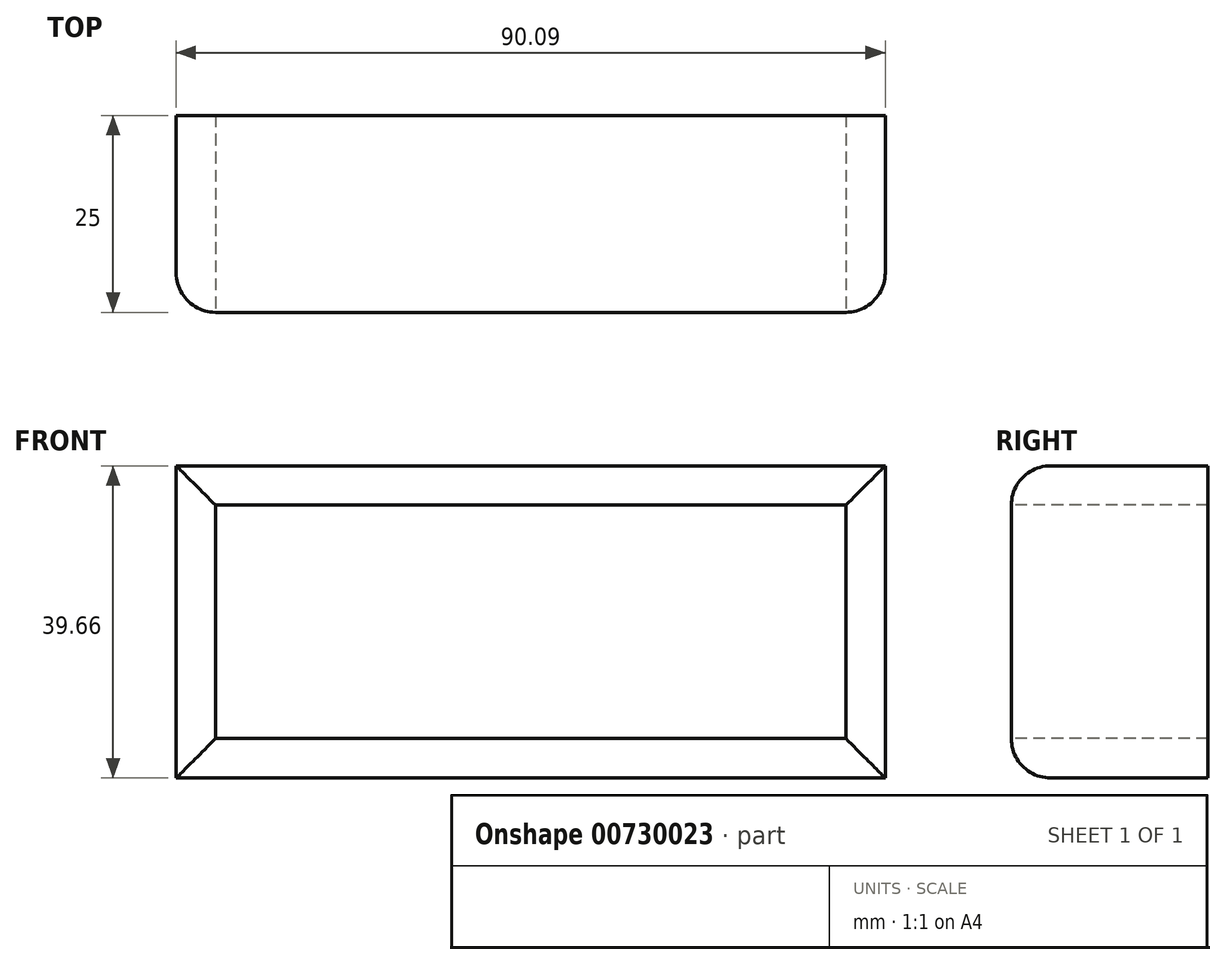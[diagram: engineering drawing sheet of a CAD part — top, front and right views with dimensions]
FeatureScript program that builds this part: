
annotation { "Feature Type Name" : "Feature", "Feature Type Description" : "" }
export const myFeature = defineFeature(function(context is Context, id is Id, definition is map)
    precondition{}
    {
        {
            var Q0;
            Q0=qCreatedBy(makeId("Front.planeOp"),FACE);
            var sketch = newSketch(context, id + "F0", { "sketchPlane" : qUnion([Q0])});
            skLineSegment(sketch, "E0.bottom", {"start": v(50, 25) * mm, "end": v(-50, 25) * mm});
            skLineSegment(sketch, "E0.top", {"start": v(50, -25) * mm, "end": v(-50, -25) * mm});
            skLineSegment(sketch, "E0.left", {"start": v(50, 25) * mm, "end": v(50, -25) * mm});
            skLineSegment(sketch, "E0.right", {"start": v(-50, 25) * mm, "end": v(-50, -25) * mm});
            skPoint(sketch, "E0.middle", {"position": v(0, 0) * mm});
            skSolve(sketch);
        }
        {
            var Q0;
            Q0=makeQuery(id+"F0.imprint","IMPRINT",FACE,{"disambiguationData":[TD([[makeQuery(id+"F0.imprint","IMPRINT",EDGE,{"derivedFrom":sQuery(id+"F0.wireOp",EDGE,"E0.bottom")}),1.0]])]});
            var sketch = newSketch(context, id + "F1", { "sketchPlane" : qUnion([Q0])});
            skSolve(sketch);
        }
        {
            var Q0;
            Q0 = qSketchRegion(id + "F1", true);
            var Q1;
            Q1=makeQuery(id+"F1.imprint","IMPRINT",FACE,{"disambiguationData":[TD([[makeQuery(id+"F1.imprint","IMPRINT",EDGE,{"derivedFrom":makeQuery(id+"F0.imprint","IMPRINT",EDGE,{"derivedFrom":sQuery(id+"F0.wireOp",EDGE,"E0.bottom")})}),1.0]])]});
            extrude(context, id + "F2", {"entities" : qUnion([Q0, Q1]), "depth" : 40 * mm, "offsetDistance" : 25 * mm});
        }
        {
            var Q0;
            Q0=makeQuery(id+"F2.opExtrude","CAP_FACE",FACE,{"disambiguationData":[OSD([sQuery(id+"F0.wireOp",EDGE,"E0.bottom"),sQuery(id+"F0.wireOp",EDGE,"E0.top"),sQuery(id+"F0.wireOp",EDGE,"E0.left"),sQuery(id+"F0.wireOp",EDGE,"E0.right")])],"isStart":false});
            var sketch = newSketch(context, id + "F3", { "sketchPlane" : qUnion([Q0])});
            skSolve(sketch);
        }
        {
            var Q0;
            Q0=makeQuery(id+"F3.imprint","IMPRINT",FACE,{"disambiguationData":[TD([[makeQuery(id+"F3.imprint","IMPRINT",EDGE,{"derivedFrom":makeQuery(id+"F2.opExtrude","CAP_EDGE",EDGE,{"disambiguationData":[OSD([sQuery(id+"F0.wireOp",EDGE,"E0.bottom")])],"isStart":false})}),1.0]])]});
            var sketch = newSketch(context, id + "F4", { "sketchPlane" : qUnion([Q0])});
            skLineSegment(sketch, "E1.bottom", {"start": v(45, 20) * mm, "end": v(-45, 20) * mm});
            skLineSegment(sketch, "E1.top", {"start": v(45, -20) * mm, "end": v(-45, -20) * mm});
            skLineSegment(sketch, "E1.left", {"start": v(45, 20) * mm, "end": v(45, -20) * mm});
            skLineSegment(sketch, "E1.right", {"start": v(-45, 20) * mm, "end": v(-45, -20) * mm});
            skPoint(sketch, "E1.middle", {"position": v(0, 0) * mm});
            skSolve(sketch);
        }
        {
            var Q0;
            Q0=makeQuery(id+"F4.imprint","IMPRINT",FACE,{"disambiguationData":[TD([[makeQuery(id+"F4.imprint","IMPRINT",EDGE,{"derivedFrom":sQuery(id+"F4.wireOp",EDGE,"E1.bottom")}),1.0]])]});
            extrude(context, id + "F5", {"entities" : qUnion([Q0]), "operationType" : NewBodyOperationType.REMOVE, "oppositeDirection" : true, "depth" : 36 * mm, "offsetDistance" : 25 * mm});
        }
        {
            var Q0;
            Q0=makeQuery(id+"F2.opExtrude","CAP_EDGE",EDGE,{"disambiguationData":[OSD([sQuery(id+"F0.wireOp",EDGE,"E0.right")])],"isStart":false});
            var Q1;
            Q1=makeQuery(id+"F2.opExtrude","CAP_EDGE",EDGE,{"disambiguationData":[OSD([sQuery(id+"F0.wireOp",EDGE,"E0.bottom")])],"isStart":false});
            var Q2;
            Q2=makeQuery(id+"F2.opExtrude","CAP_EDGE",EDGE,{"disambiguationData":[OSD([sQuery(id+"F0.wireOp",EDGE,"E0.left")])],"isStart":false});
            var Q3;
            Q3=makeQuery(id+"F2.opExtrude","CAP_EDGE",EDGE,{"disambiguationData":[OSD([sQuery(id+"F0.wireOp",EDGE,"E0.top")])],"isStart":false});
            fillet(context, id + "F6", {"entities" : qUnion([Q0, Q1, Q2, Q3]), "radius" : 5 * mm, "tangentPropagation" : true, "allowEdgeOverflow" : false});
        }
        {
            var Q0;
            Q0=makeQuery(id+"F3.imprint","IMPRINT",FACE,{"disambiguationData":[TD([[makeQuery(id+"F3.imprint","IMPRINT",EDGE,{"derivedFrom":makeQuery(id+"F2.opExtrude","CAP_EDGE",EDGE,{"disambiguationData":[OSD([sQuery(id+"F0.wireOp",EDGE,"E0.bottom")])],"isStart":false})}),1.0]])]});
            var sketch = newSketch(context, id + "F7", { "sketchPlane" : qUnion([Q0])});
            skSolve(sketch);
        }
        {
            var Q0;
            Q0=makeQuery(id+"F2.opExtrude","SWEPT_FACE",FACE,{"disambiguationData":[OSD([sQuery(id+"F0.wireOp",EDGE,"E0.top")])]});
            var sketch = newSketch(context, id + "F8", { "sketchPlane" : qUnion([Q0])});
            skText(sketch, "E2", { "text": "Jonas", "fontName": "OpenSans-Regular.ttf"});
            const initialGuessF8  = {"E2": [-0.0245, 0.01127, 1, 0, 0.01358]};
            skSetInitialGuess(sketch, initialGuessF8);
            skSolve(sketch);
        }
        {
            var Q0;
            Q0 = qSketchRegion(id + "F8", true);
            extrude(context, id + "F9", {"entities" : qUnion([Q0]), "operationType" : NewBodyOperationType.REMOVE, "oppositeDirection" : true, "depth" : 5.7 * mm, "offsetDistance" : 25 * mm});
        }
        {
            var Q0;
            Q0=makeQuery(id+"F7.imprint","IMPRINT",FACE,{"disambiguationData":[TD([[makeQuery(id+"F7.imprint","IMPRINT",EDGE,{"derivedFrom":makeQuery(id+"F3.imprint","IMPRINT",EDGE,{"derivedFrom":makeQuery(id+"F2.opExtrude","CAP_EDGE",EDGE,{"disambiguationData":[OSD([sQuery(id+"F0.wireOp",EDGE,"E0.bottom")])],"isStart":false})})}),1.0]])]});
            var sketch = newSketch(context, id + "F10", { "sketchPlane" : qUnion([Q0])});
            skLineSegment(sketch, "E3.bottom", {"start": v(-45.47, 19.97) * mm, "end": v(44.62, 19.97) * mm});
            skLineSegment(sketch, "E3.top", {"start": v(-45.47, -19.69) * mm, "end": v(44.62, -19.69) * mm});
            skLineSegment(sketch, "E3.left", {"start": v(-45.47, 19.97) * mm, "end": v(-45.47, -19.69) * mm});
            skLineSegment(sketch, "E3.right", {"start": v(44.62, 19.97) * mm, "end": v(44.62, -19.69) * mm});
            skSolve(sketch);
        }
        {
            var Q0;
            Q0 = qSketchRegion(id + "F10", true);
            extrude(context, id + "F11", {"entities" : qUnion([Q0]), "depth" : 25 * mm, "offsetDistance" : 25 * mm});
        }
        {
            var Q0;
            Q0=makeQuery(id+"F11.opExtrude","CAP_EDGE",EDGE,{"disambiguationData":[OSD([sQuery(id+"F10.wireOp",EDGE,"E3.top")])],"isStart":false});
            var Q1;
            Q1=makeQuery(id+"F11.opExtrude","CAP_EDGE",EDGE,{"disambiguationData":[OSD([sQuery(id+"F10.wireOp",EDGE,"E3.left")])],"isStart":false});
            var Q2;
            Q2=makeQuery(id+"F11.opExtrude","CAP_EDGE",EDGE,{"disambiguationData":[OSD([sQuery(id+"F10.wireOp",EDGE,"E3.bottom")])],"isStart":false});
            var Q3;
            Q3=makeQuery(id+"F11.opExtrude","CAP_EDGE",EDGE,{"disambiguationData":[OSD([sQuery(id+"F10.wireOp",EDGE,"E3.right")])],"isStart":false});
            fillet(context, id + "F12", {"entities" : qUnion([Q0, Q1, Q2, Q3]), "radius" : 5 * mm, "tangentPropagation" : true, "allowEdgeOverflow" : false});
        }
        {
            var Q0;
            Q0=makeQuery(id+"F11.opExtrude","CAP_FACE",FACE,{"disambiguationData":[OSD([sQuery(id+"F10.wireOp",EDGE,"E3.bottom"),sQuery(id+"F10.wireOp",EDGE,"E3.top"),sQuery(id+"F10.wireOp",EDGE,"E3.left"),sQuery(id+"F10.wireOp",EDGE,"E3.right")])],"isStart":false});
            var sketch = newSketch(context, id + "F13", { "sketchPlane" : qUnion([Q0])});
            skLineSegment(sketch, "E4.bottom", {"start": v(-40.47, 14.97) * mm, "end": v(39.62, 14.97) * mm});
            skLineSegment(sketch, "E4.top", {"start": v(-40.47, -14.69) * mm, "end": v(39.62, -14.69) * mm});
            skLineSegment(sketch, "E4.left", {"start": v(-40.47, 14.97) * mm, "end": v(-40.47, -14.69) * mm});
            skLineSegment(sketch, "E4.right", {"start": v(39.62, 14.97) * mm, "end": v(39.62, -14.69) * mm});
            skSolve(sketch);
        }
        {
            var Q0;
            Q0 = qSketchRegion(id + "F13", true);
            extrude(context, id + "F14", {"entities" : qUnion([Q0]), "operationType" : NewBodyOperationType.REMOVE, "oppositeDirection" : true, "depth" : 60 * mm, "offsetDistance" : 25 * mm});
        }
        {
            var Q0;
            Q0=makeQuery(id+"F9.boolean.opBoolean","SPLIT",BODY,{"disambiguationData":[OD(0.0)],"derivedFrom":makeQuery(id+"F2.opExtrude","SWEPT_BODY",BODY,{"disambiguationData":[OSD([sQuery(id+"F0.wireOp",EDGE,"E0.bottom"),sQuery(id+"F0.wireOp",EDGE,"E0.top"),sQuery(id+"F0.wireOp",EDGE,"E0.left"),sQuery(id+"F0.wireOp",EDGE,"E0.right")])]})});
            deleteBodies(context, id + "F15", {"entities" : qUnion([Q0])});
        }
    });
